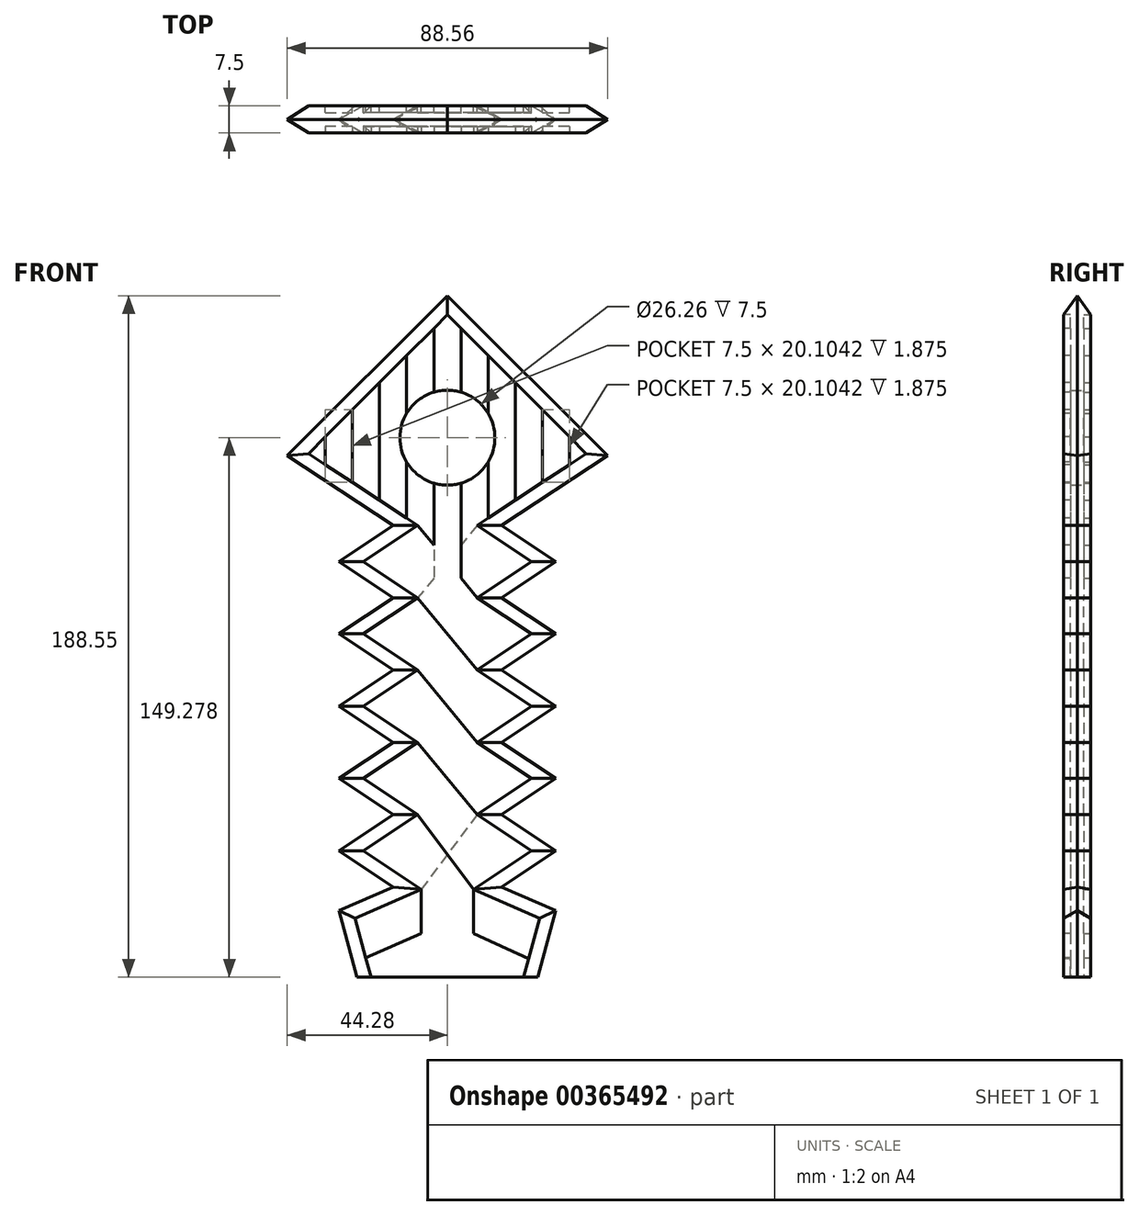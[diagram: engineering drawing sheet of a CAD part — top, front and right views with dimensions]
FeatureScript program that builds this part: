
annotation { "Feature Type Name" : "Feature", "Feature Type Description" : "" }
export const myFeature = defineFeature(function(context is Context, id is Id, definition is map)
    precondition{}
    {
        {
            var Q0;
            Q0=qCreatedBy(makeId("Front.planeOp"),FACE);
            var sketch = newSketch(context, id + "F0", { "sketchPlane" : qUnion([Q0])});
            skLineSegment(sketch, "E0", {"start": v(-15, -50) * mm, "end": v(15, -50) * mm});
            skLineSegment(sketch, "E1", {"start": v(15, -50) * mm, "end": v(15, 75) * mm});
            skLineSegment(sketch, "E2", {"start": v(-15, 75) * mm, "end": v(-15, -50) * mm});
            skLineSegment(sketch, "E3", {"start": v(15, 75) * mm, "end": v(34.28, 94.28) * mm});
            skLineSegment(sketch, "E4", {"start": v(34.28, 94.28) * mm, "end": v(0, 128.55) * mm});
            skLineSegment(sketch, "E5", {"start": v(0, 128.55) * mm, "end": v(-34.28, 94.28) * mm});
            skLineSegment(sketch, "E6", {"start": v(-15, 75) * mm, "end": v(-34.28, 94.28) * mm});
            skLineSegment(sketch, "E7", {"start": v(0, 128.55) * mm, "end": v(0, 138.55) * mm});
            skLineSegment(sketch, "E8", {"start": v(0, 138.55) * mm, "end": v(44.28, 94.28) * mm});
            skLineSegment(sketch, "E9", {"start": v(44.28, 94.28) * mm, "end": v(15, 75) * mm});
            skLineSegment(sketch, "E10", {"start": v(0, 138.55) * mm, "end": v(-44.28, 94.28) * mm});
            skLineSegment(sketch, "E11", {"start": v(-44.28, 94.28) * mm, "end": v(-15, 75) * mm});
            skLineSegment(sketch, "E12", {"start": v(-34.28, 94.28) * mm, "end": v(-44.28, 94.28) * mm});
            skLineSegment(sketch, "E13", {"start": v(34.28, 94.28) * mm, "end": v(44.28, 94.28) * mm});
            skLineSegment(sketch, "E14", {"start": v(15, 75) * mm, "end": v(25, 65) * mm});
            skLineSegment(sketch, "E15", {"start": v(25, 65) * mm, "end": v(15, 55) * mm});
            skLineSegment(sketch, "E16", {"start": v(15, 55) * mm, "end": v(25, 45) * mm});
            skLineSegment(sketch, "E17", {"start": v(25, 45) * mm, "end": v(15, 35) * mm});
            skLineSegment(sketch, "E18", {"start": v(15, 35) * mm, "end": v(25, 25) * mm});
            skLineSegment(sketch, "E19", {"start": v(25, 25) * mm, "end": v(15, 15) * mm});
            skLineSegment(sketch, "E20", {"start": v(15, 15) * mm, "end": v(25, 5) * mm});
            skLineSegment(sketch, "E21", {"start": v(25, 5) * mm, "end": v(15, -5) * mm});
            skLineSegment(sketch, "E22", {"start": v(15, -5) * mm, "end": v(25, -15) * mm});
            skLineSegment(sketch, "E23", {"start": v(25, -15) * mm, "end": v(15, -25) * mm});
            skLineSegment(sketch, "E24", {"start": v(15, 75) * mm, "end": v(30, 65) * mm});
            skLineSegment(sketch, "E25", {"start": v(30, 65) * mm, "end": v(15, 55) * mm});
            skLineSegment(sketch, "E26", {"start": v(15, 55) * mm, "end": v(30, 45) * mm});
            skLineSegment(sketch, "E27", {"start": v(30, 45) * mm, "end": v(15, 35) * mm});
            skLineSegment(sketch, "E28", {"start": v(15, 35) * mm, "end": v(30, 25) * mm});
            skLineSegment(sketch, "E29", {"start": v(30, 25) * mm, "end": v(15, 15) * mm});
            skLineSegment(sketch, "E30", {"start": v(15, 15) * mm, "end": v(30, 5) * mm});
            skLineSegment(sketch, "E31", {"start": v(30, 5) * mm, "end": v(15, -5) * mm});
            skLineSegment(sketch, "E32", {"start": v(15, -5) * mm, "end": v(30, -15) * mm});
            skLineSegment(sketch, "E33", {"start": v(30, -15) * mm, "end": v(15, -25) * mm});
            skLineSegment(sketch, "E34", {"start": v(15, -25) * mm, "end": v(30, -31.56) * mm});
            skLineSegment(sketch, "E35", {"start": v(30, -31.56) * mm, "end": v(25, -50) * mm});
            skLineSegment(sketch, "E36", {"start": v(25, -50) * mm, "end": v(15, -50) * mm});
            skLineSegment(sketch, "E37", {"start": v(-15, 75) * mm, "end": v(-25, 65) * mm});
            skLineSegment(sketch, "E38", {"start": v(-25, 65) * mm, "end": v(-15, 55) * mm});
            skLineSegment(sketch, "E39", {"start": v(-15, 55) * mm, "end": v(-25, 45) * mm});
            skLineSegment(sketch, "E40", {"start": v(-25, 45) * mm, "end": v(-15, 35) * mm});
            skLineSegment(sketch, "E41", {"start": v(-15, 35) * mm, "end": v(-25, 25) * mm});
            skLineSegment(sketch, "E42", {"start": v(-25, 25) * mm, "end": v(-15, 15) * mm});
            skLineSegment(sketch, "E43", {"start": v(-15, 15) * mm, "end": v(-25, 5) * mm});
            skLineSegment(sketch, "E44", {"start": v(-25, 5) * mm, "end": v(-15, -5) * mm});
            skLineSegment(sketch, "E45", {"start": v(-15, -5) * mm, "end": v(-25, -15) * mm});
            skLineSegment(sketch, "E46", {"start": v(-25, -15) * mm, "end": v(-15, -25) * mm});
            skLineSegment(sketch, "E47", {"start": v(-15, 75) * mm, "end": v(-30, 65) * mm});
            skLineSegment(sketch, "E48", {"start": v(-30, 65) * mm, "end": v(-15, 55) * mm});
            skLineSegment(sketch, "E49", {"start": v(-15, 55) * mm, "end": v(-30, 45) * mm});
            skLineSegment(sketch, "E50", {"start": v(-30, 45) * mm, "end": v(-15, 35) * mm});
            skLineSegment(sketch, "E51", {"start": v(-15, 35) * mm, "end": v(-30, 25) * mm});
            skLineSegment(sketch, "E52", {"start": v(-30, 25) * mm, "end": v(-15, 15) * mm});
            skLineSegment(sketch, "E53", {"start": v(-15, 15) * mm, "end": v(-30, 5) * mm});
            skLineSegment(sketch, "E54", {"start": v(-30, 5) * mm, "end": v(-15, -5) * mm});
            skLineSegment(sketch, "E55", {"start": v(-15, -5) * mm, "end": v(-30, -15) * mm});
            skLineSegment(sketch, "E56", {"start": v(-30, -15) * mm, "end": v(-15, -25) * mm});
            skLineSegment(sketch, "E57", {"start": v(-15, -25) * mm, "end": v(-30, -31.56) * mm});
            skLineSegment(sketch, "E58", {"start": v(-30, -31.56) * mm, "end": v(-25, -50) * mm});
            skLineSegment(sketch, "E59", {"start": v(-25, -50) * mm, "end": v(-15, -50) * mm});
            skCircle(sketch, "E60", {"center": v(0, 99.28) * mm, "radius": 13.13 * mm});
            skLineSegment(sketch, "E61", {"start": v(3.75, 86.7) * mm, "end": v(3.75, -50) * mm});
            skLineSegment(sketch, "E62", {"start": v(-3.75, 86.7) * mm, "end": v(-3.75, -50) * mm});
            skSolve(sketch);
        }
        {
            var Q0;
            Q0 = qSketchRegion(id + "F0", true);
            var Q1;
            Q1=makeQuery(id+"F0.imprint","IMPRINT",FACE,{"disambiguationData":[TD([[makeQuery(id+"F0.imprint","IMPRINT",EDGE,{"derivedFrom":sQuery(id+"F0.wireOp",EDGE,"tEIcV5ed-Dlti-Xe9K-ipyq-D6JpYmqXNQwO")}),-1.0]])]});
            var Q2;
            Q2=makeQuery(id+"F0.imprint","IMPRINT",FACE,{"disambiguationData":[TD([[makeQuery(id+"F0.imprint","IMPRINT",EDGE,{"derivedFrom":sQuery(id+"F0.wireOp",EDGE,"oY2jZxbk-D1su-Rdax-I2aS-zYsjSGYaF0MI")}),-1.0]])]});
            var Q3;
            Q3=makeQuery(id+"F0.imprint","IMPRINT",FACE,{"disambiguationData":[TD([[makeQuery(id+"F0.imprint","IMPRINT",EDGE,{"derivedFrom":sQuery(id+"F0.wireOp",EDGE,"hQpNWvsG-qMPW-6KJk-tWaw-b78FssZYuDap")}),-1.0]])]});
            extrude(context, id + "F1", {"entities" : qUnion([Q0, Q1, Q2, Q3]), "depth" : 7.5 * mm});
        }
        {
            var Q0;
            Q0=makeQuery(id+"F1.opExtrude","CAP_EDGE",EDGE,{"disambiguationData":[OSD([sQuery(id+"F0.wireOp",EDGE,"E10")])],"isStart":false});
            var Q1;
            Q1=makeQuery(id+"F1.opExtrude","CAP_EDGE",EDGE,{"disambiguationData":[OSD([sQuery(id+"F0.wireOp",EDGE,"E8")])],"isStart":true});
            var Q2;
            Q2=makeQuery(id+"F1.opExtrude","CAP_EDGE",EDGE,{"disambiguationData":[OSD([sQuery(id+"F0.wireOp",EDGE,"E10")])],"isStart":true});
            var Q3;
            Q3=makeQuery(id+"F1.opExtrude","CAP_EDGE",EDGE,{"disambiguationData":[OSD([sQuery(id+"F0.wireOp",EDGE,"E8")])],"isStart":false});
            var Q4;
            Q4=makeQuery(id+"F1.opExtrude","CAP_EDGE",EDGE,{"disambiguationData":[OSD([sQuery(id+"F0.wireOp",EDGE,"E9")])],"isStart":false});
            var Q5;
            Q5=makeQuery(id+"F1.opExtrude","CAP_EDGE",EDGE,{"disambiguationData":[OSD([sQuery(id+"F0.wireOp",EDGE,"E9")])],"isStart":true});
            var Q6;
            Q6=makeQuery(id+"F1.opExtrude","CAP_EDGE",EDGE,{"disambiguationData":[OSD([sQuery(id+"F0.wireOp",EDGE,"E11")])],"isStart":true});
            var Q7;
            Q7=makeQuery(id+"F1.opExtrude","CAP_EDGE",EDGE,{"disambiguationData":[OSD([sQuery(id+"F0.wireOp",EDGE,"E11")])],"isStart":false});
            var Q8;
            Q8=makeQuery(id+"F1.opExtrude","CAP_EDGE",EDGE,{"disambiguationData":[OSD([sQuery(id+"F0.wireOp",EDGE,"E24")])],"isStart":true});
            var Q9;
            Q9=makeQuery(id+"F1.opExtrude","CAP_EDGE",EDGE,{"disambiguationData":[OSD([sQuery(id+"F0.wireOp",EDGE,"E25")])],"isStart":true});
            var Q10;
            Q10=makeQuery(id+"F1.opExtrude","CAP_EDGE",EDGE,{"disambiguationData":[OSD([sQuery(id+"F0.wireOp",EDGE,"E26")])],"isStart":true});
            var Q11;
            Q11=makeQuery(id+"F1.opExtrude","CAP_EDGE",EDGE,{"disambiguationData":[OSD([sQuery(id+"F0.wireOp",EDGE,"E27")])],"isStart":true});
            var Q12;
            Q12=makeQuery(id+"F1.opExtrude","CAP_EDGE",EDGE,{"disambiguationData":[OSD([sQuery(id+"F0.wireOp",EDGE,"E28")])],"isStart":true});
            var Q13;
            Q13=makeQuery(id+"F1.opExtrude","CAP_EDGE",EDGE,{"disambiguationData":[OSD([sQuery(id+"F0.wireOp",EDGE,"E29")])],"isStart":true});
            var Q14;
            Q14=makeQuery(id+"F1.opExtrude","CAP_EDGE",EDGE,{"disambiguationData":[OSD([sQuery(id+"F0.wireOp",EDGE,"E30")])],"isStart":true});
            var Q15;
            Q15=makeQuery(id+"F1.opExtrude","CAP_EDGE",EDGE,{"disambiguationData":[OSD([sQuery(id+"F0.wireOp",EDGE,"E31")])],"isStart":true});
            var Q16;
            Q16=makeQuery(id+"F1.opExtrude","CAP_EDGE",EDGE,{"disambiguationData":[OSD([sQuery(id+"F0.wireOp",EDGE,"E32")])],"isStart":true});
            var Q17;
            Q17=makeQuery(id+"F1.opExtrude","CAP_EDGE",EDGE,{"disambiguationData":[OSD([sQuery(id+"F0.wireOp",EDGE,"E33")])],"isStart":true});
            var Q18;
            Q18=makeQuery(id+"F1.opExtrude","CAP_EDGE",EDGE,{"disambiguationData":[OSD([sQuery(id+"F0.wireOp",EDGE,"E24")])],"isStart":false});
            var Q19;
            Q19=makeQuery(id+"F1.opExtrude","CAP_EDGE",EDGE,{"disambiguationData":[OSD([sQuery(id+"F0.wireOp",EDGE,"E25")])],"isStart":false});
            var Q20;
            Q20=makeQuery(id+"F1.opExtrude","CAP_EDGE",EDGE,{"disambiguationData":[OSD([sQuery(id+"F0.wireOp",EDGE,"E26")])],"isStart":false});
            var Q21;
            Q21=makeQuery(id+"F1.opExtrude","CAP_EDGE",EDGE,{"disambiguationData":[OSD([sQuery(id+"F0.wireOp",EDGE,"E27")])],"isStart":false});
            var Q22;
            Q22=makeQuery(id+"F1.opExtrude","CAP_EDGE",EDGE,{"disambiguationData":[OSD([sQuery(id+"F0.wireOp",EDGE,"E28")])],"isStart":false});
            var Q23;
            Q23=makeQuery(id+"F1.opExtrude","CAP_EDGE",EDGE,{"disambiguationData":[OSD([sQuery(id+"F0.wireOp",EDGE,"E29")])],"isStart":false});
            var Q24;
            Q24=makeQuery(id+"F1.opExtrude","CAP_EDGE",EDGE,{"disambiguationData":[OSD([sQuery(id+"F0.wireOp",EDGE,"E30")])],"isStart":false});
            var Q25;
            Q25=makeQuery(id+"F1.opExtrude","CAP_EDGE",EDGE,{"disambiguationData":[OSD([sQuery(id+"F0.wireOp",EDGE,"E31")])],"isStart":false});
            var Q26;
            Q26=makeQuery(id+"F1.opExtrude","CAP_EDGE",EDGE,{"disambiguationData":[OSD([sQuery(id+"F0.wireOp",EDGE,"E32")])],"isStart":false});
            var Q27;
            Q27=makeQuery(id+"F1.opExtrude","CAP_EDGE",EDGE,{"disambiguationData":[OSD([sQuery(id+"F0.wireOp",EDGE,"E33")])],"isStart":false});
            var Q28;
            Q28=makeQuery(id+"F1.opExtrude","CAP_EDGE",EDGE,{"disambiguationData":[OSD([sQuery(id+"F0.wireOp",EDGE,"E47")])],"isStart":false});
            var Q29;
            Q29=makeQuery(id+"F1.opExtrude","CAP_EDGE",EDGE,{"disambiguationData":[OSD([sQuery(id+"F0.wireOp",EDGE,"E48")])],"isStart":false});
            var Q30;
            Q30=makeQuery(id+"F1.opExtrude","CAP_EDGE",EDGE,{"disambiguationData":[OSD([sQuery(id+"F0.wireOp",EDGE,"E49")])],"isStart":false});
            var Q31;
            Q31=makeQuery(id+"F1.opExtrude","CAP_EDGE",EDGE,{"disambiguationData":[OSD([sQuery(id+"F0.wireOp",EDGE,"E50")])],"isStart":false});
            var Q32;
            Q32=makeQuery(id+"F1.opExtrude","CAP_EDGE",EDGE,{"disambiguationData":[OSD([sQuery(id+"F0.wireOp",EDGE,"E51")])],"isStart":false});
            var Q33;
            Q33=makeQuery(id+"F1.opExtrude","CAP_EDGE",EDGE,{"disambiguationData":[OSD([sQuery(id+"F0.wireOp",EDGE,"E52")])],"isStart":false});
            var Q34;
            Q34=makeQuery(id+"F1.opExtrude","CAP_EDGE",EDGE,{"disambiguationData":[OSD([sQuery(id+"F0.wireOp",EDGE,"E53")])],"isStart":false});
            var Q35;
            Q35=makeQuery(id+"F1.opExtrude","CAP_EDGE",EDGE,{"disambiguationData":[OSD([sQuery(id+"F0.wireOp",EDGE,"E54")])],"isStart":false});
            var Q36;
            Q36=makeQuery(id+"F1.opExtrude","CAP_EDGE",EDGE,{"disambiguationData":[OSD([sQuery(id+"F0.wireOp",EDGE,"E55")])],"isStart":false});
            var Q37;
            Q37=makeQuery(id+"F1.opExtrude","CAP_EDGE",EDGE,{"disambiguationData":[OSD([sQuery(id+"F0.wireOp",EDGE,"E56")])],"isStart":false});
            var Q38;
            Q38=makeQuery(id+"F1.opExtrude","CAP_EDGE",EDGE,{"disambiguationData":[OSD([sQuery(id+"F0.wireOp",EDGE,"E57")])],"isStart":false});
            var Q39;
            Q39=makeQuery(id+"F1.opExtrude","CAP_EDGE",EDGE,{"disambiguationData":[OSD([sQuery(id+"F0.wireOp",EDGE,"E47")])],"isStart":true});
            var Q40;
            Q40=makeQuery(id+"F1.opExtrude","CAP_EDGE",EDGE,{"disambiguationData":[OSD([sQuery(id+"F0.wireOp",EDGE,"E48")])],"isStart":true});
            var Q41;
            Q41=makeQuery(id+"F1.opExtrude","CAP_EDGE",EDGE,{"disambiguationData":[OSD([sQuery(id+"F0.wireOp",EDGE,"E49")])],"isStart":true});
            var Q42;
            Q42=makeQuery(id+"F1.opExtrude","CAP_EDGE",EDGE,{"disambiguationData":[OSD([sQuery(id+"F0.wireOp",EDGE,"E50")])],"isStart":true});
            var Q43;
            Q43=makeQuery(id+"F1.opExtrude","CAP_EDGE",EDGE,{"disambiguationData":[OSD([sQuery(id+"F0.wireOp",EDGE,"E51")])],"isStart":true});
            var Q44;
            Q44=makeQuery(id+"F1.opExtrude","CAP_EDGE",EDGE,{"disambiguationData":[OSD([sQuery(id+"F0.wireOp",EDGE,"E52")])],"isStart":true});
            var Q45;
            Q45=makeQuery(id+"F1.opExtrude","CAP_EDGE",EDGE,{"disambiguationData":[OSD([sQuery(id+"F0.wireOp",EDGE,"E53")])],"isStart":true});
            var Q46;
            Q46=makeQuery(id+"F1.opExtrude","CAP_EDGE",EDGE,{"disambiguationData":[OSD([sQuery(id+"F0.wireOp",EDGE,"E54")])],"isStart":true});
            var Q47;
            Q47=makeQuery(id+"F1.opExtrude","CAP_EDGE",EDGE,{"disambiguationData":[OSD([sQuery(id+"F0.wireOp",EDGE,"E55")])],"isStart":true});
            var Q48;
            Q48=makeQuery(id+"F1.opExtrude","CAP_EDGE",EDGE,{"disambiguationData":[OSD([sQuery(id+"F0.wireOp",EDGE,"E56")])],"isStart":true});
            var Q49;
            Q49=makeQuery(id+"F1.opExtrude","CAP_EDGE",EDGE,{"disambiguationData":[OSD([sQuery(id+"F0.wireOp",EDGE,"E34")])],"isStart":false});
            var Q50;
            Q50=makeQuery(id+"F1.opExtrude","CAP_EDGE",EDGE,{"disambiguationData":[OSD([sQuery(id+"F0.wireOp",EDGE,"E34")])],"isStart":true});
            var Q51;
            Q51=makeQuery(id+"F1.opExtrude","CAP_EDGE",EDGE,{"disambiguationData":[OSD([sQuery(id+"F0.wireOp",EDGE,"E57")])],"isStart":true});
            var Q52;
            Q52=makeQuery(id+"F1.opExtrude","CAP_EDGE",EDGE,{"disambiguationData":[OSD([sQuery(id+"F0.wireOp",EDGE,"E58")])],"isStart":false});
            var Q53;
            Q53=makeQuery(id+"F1.opExtrude","CAP_EDGE",EDGE,{"disambiguationData":[OSD([sQuery(id+"F0.wireOp",EDGE,"E35")])],"isStart":false});
            var Q54;
            Q54=makeQuery(id+"F1.opExtrude","CAP_EDGE",EDGE,{"disambiguationData":[OSD([sQuery(id+"F0.wireOp",EDGE,"E35")])],"isStart":true});
            var Q55;
            Q55=makeQuery(id+"F1.opExtrude","CAP_EDGE",EDGE,{"disambiguationData":[OSD([sQuery(id+"F0.wireOp",EDGE,"E58")])],"isStart":true});
            chamfer(context, id + "F2", {"entities" : qUnion([Q0, Q1, Q2, Q3, Q4, Q5, Q6, Q7, Q8, Q9, Q10, Q11, Q12, Q13, Q14, Q15, Q16, Q17, Q18, Q19, Q20, Q21, Q22, Q23, Q24, Q25, Q26, Q27, Q28, Q29, Q30, Q31, Q32, Q33, Q34, Q35, Q36, Q37, Q38, Q39, Q40, Q41, Q42, Q43, Q44, Q45, Q46, Q47, Q48, Q49, Q50, Q51, Q52, Q53, Q54, Q55]), "width" : 3.75 * mm, "tangentPropagation" : true});
        }
        {
            var Q0;
            Q0=makeQuery(id+"F1.opExtrude","CAP_FACE",FACE,{"disambiguationData":[OSD([sQuery(id+"F0.wireOp",EDGE,"E0"),sQuery(id+"F0.wireOp",EDGE,"E8"),sQuery(id+"F0.wireOp",EDGE,"E9"),sQuery(id+"F0.wireOp",EDGE,"E10"),sQuery(id+"F0.wireOp",EDGE,"E11"),sQuery(id+"F0.wireOp",EDGE,"E24"),sQuery(id+"F0.wireOp",EDGE,"E25"),sQuery(id+"F0.wireOp",EDGE,"E26"),sQuery(id+"F0.wireOp",EDGE,"E27"),sQuery(id+"F0.wireOp",EDGE,"E28"),sQuery(id+"F0.wireOp",EDGE,"E29"),sQuery(id+"F0.wireOp",EDGE,"E30"),sQuery(id+"F0.wireOp",EDGE,"E31"),sQuery(id+"F0.wireOp",EDGE,"E32"),sQuery(id+"F0.wireOp",EDGE,"E33"),sQuery(id+"F0.wireOp",EDGE,"E34"),sQuery(id+"F0.wireOp",EDGE,"E35"),sQuery(id+"F0.wireOp",EDGE,"E36"),sQuery(id+"F0.wireOp",EDGE,"E47"),sQuery(id+"F0.wireOp",EDGE,"E48"),sQuery(id+"F0.wireOp",EDGE,"E49"),sQuery(id+"F0.wireOp",EDGE,"E50"),sQuery(id+"F0.wireOp",EDGE,"E51"),sQuery(id+"F0.wireOp",EDGE,"E52"),sQuery(id+"F0.wireOp",EDGE,"E53"),sQuery(id+"F0.wireOp",EDGE,"E54"),sQuery(id+"F0.wireOp",EDGE,"E55"),sQuery(id+"F0.wireOp",EDGE,"E56"),sQuery(id+"F0.wireOp",EDGE,"E57"),sQuery(id+"F0.wireOp",EDGE,"E58"),sQuery(id+"F0.wireOp",EDGE,"E59"),sQuery(id+"F0.wireOp",EDGE,"E60")])],"isStart":true});
            var sketch = newSketch(context, id + "F3", { "sketchPlane" : qUnion([Q0])});
            skLineSegment(sketch, "E63", {"start": v(3.75, 129.5) * mm, "end": v(3.75, 86.7) * mm});
            skLineSegment(sketch, "E64", {"start": v(-3.75, 129.5) * mm, "end": v(-3.75, 86.7) * mm});
            skLineSegment(sketch, "E65", {"start": v(11.25, 122) * mm, "end": v(11.25, 77.02) * mm});
            skLineSegment(sketch, "E66", {"start": v(18.75, 114.5) * mm, "end": v(18.75, 81.96) * mm});
            skLineSegment(sketch, "E67", {"start": v(26.25, 107) * mm, "end": v(26.25, 86.9) * mm});
            skLineSegment(sketch, "E68", {"start": v(-11.25, 122) * mm, "end": v(-11.25, 77.02) * mm});
            skLineSegment(sketch, "E69", {"start": v(-18.75, 114.5) * mm, "end": v(-18.75, 81.96) * mm});
            skLineSegment(sketch, "E70", {"start": v(-26.25, 107) * mm, "end": v(-26.25, 86.9) * mm});
            skLineSegment(sketch, "E71", {"start": v(-33.75, 99.5) * mm, "end": v(-33.75, 91.84) * mm});
            skLineSegment(sketch, "E72", {"start": v(33.75, 99.5) * mm, "end": v(33.75, 91.84) * mm});
            skLineSegment(sketch, "E73", {"start": v(-8.24, -5) * mm, "end": v(7.2, -25.69) * mm});
            skLineSegment(sketch, "E74", {"start": v(7.2, -25.69) * mm, "end": v(-7.2, -25.69) * mm});
            skLineSegment(sketch, "E75", {"start": v(-7.2, -25.69) * mm, "end": v(8.24, -5) * mm});
            skLineSegment(sketch, "E76", {"start": v(8.24, -5) * mm, "end": v(-8.24, 15) * mm});
            skLineSegment(sketch, "E77", {"start": v(-8.24, 15) * mm, "end": v(8.24, 35) * mm});
            skLineSegment(sketch, "E78", {"start": v(8.24, 35) * mm, "end": v(-8.24, 55) * mm});
            skLineSegment(sketch, "E79", {"start": v(-8.24, 55) * mm, "end": v(8.21, 75.02) * mm});
            skLineSegment(sketch, "E80", {"start": v(-8.21, 75.02) * mm, "end": v(8.21, 75.02) * mm});
            skLineSegment(sketch, "E81", {"start": v(-8.21, 75.02) * mm, "end": v(8.24, 55) * mm});
            skLineSegment(sketch, "E82", {"start": v(8.24, 55) * mm, "end": v(-8.24, 35) * mm});
            skLineSegment(sketch, "E83", {"start": v(-8.24, 35) * mm, "end": v(8.24, 15) * mm});
            skLineSegment(sketch, "E84", {"start": v(8.24, 15) * mm, "end": v(-8.24, -5) * mm});
            skLineSegment(sketch, "E85", {"start": v(-3.75, 86.7) * mm, "end": v(-3.75, 75.02) * mm});
            skLineSegment(sketch, "E86", {"start": v(3.75, 86.7) * mm, "end": v(3.75, 75.02) * mm});
            skLineSegment(sketch, "E87", {"start": v(-3.75, 75.02) * mm, "end": v(-3.75, 69.6) * mm});
            skLineSegment(sketch, "E88", {"start": v(3.75, 75.02) * mm, "end": v(3.75, 60.46) * mm});
            skLineSegment(sketch, "E89", {"start": v(-7.2, -50) * mm, "end": v(-7.2, -25.69) * mm});
            skLineSegment(sketch, "E90", {"start": v(7.2, -25.69) * mm, "end": v(7.2, -50) * mm});
            skLineSegment(sketch, "E91", {"start": v(7.2, -37.84) * mm, "end": v(26.06, -46.08) * mm});
            skLineSegment(sketch, "E92", {"start": v(-7.2, -37.84) * mm, "end": v(-26.06, -46.08) * mm});
            skSolve(sketch);
        }
        {
            var Q0;
            {var subQ0=sQuery(id+"F0.wireOp",EDGE,"E60");var subQ7=sQuery(id+"F3.wireOp",EDGE,"E63");var subQ9=makeQuery(id+"F1.opExtrude","CAP_EDGE",EDGE,{"disambiguationData":[OSD([subQ0])],"isStart":true});var subQ10=makeQuery(id+"F3.imprint","INTERSECT",VERTEX,{"disambiguationData":[OD(1.0)],"derivedFrom":[subQ9,subQ7]});Q0=makeQuery(id+"F3.imprint","IMPRINT",FACE,{"disambiguationData":[TD([[makeQuery(id+"F3.imprint","IMPRINT",EDGE,{"disambiguationData":[TD([[subQ10,1.0]])],"derivedFrom":subQ9}),1.0]])]});}
            var Q1;
            {var subQ7=sQuery(id+"F3.wireOp",EDGE,"E66");Q1=makeQuery(id+"F3.imprint","IMPRINT",FACE,{"disambiguationData":[TD([[makeQuery(id+"F3.imprint","IMPRINT",EDGE,{"derivedFrom":subQ7}),-1.0]])]});}
            var Q2;
            {var subQ0=sQuery(id+"F3.wireOp",EDGE,"E67");Q2=makeQuery(id+"F3.imprint","IMPRINT",FACE,{"disambiguationData":[TD([[makeQuery(id+"F3.imprint","IMPRINT",EDGE,{"derivedFrom":subQ0}),1.0]])]});}
            var Q3;
            {var subQ0=sQuery(id+"F3.wireOp",EDGE,"E69");Q3=makeQuery(id+"F3.imprint","IMPRINT",FACE,{"disambiguationData":[TD([[makeQuery(id+"F3.imprint","IMPRINT",EDGE,{"derivedFrom":subQ0}),1.0]])]});}
            var Q4;
            {var subQ0=sQuery(id+"F3.wireOp",EDGE,"E70");Q4=makeQuery(id+"F3.imprint","IMPRINT",FACE,{"disambiguationData":[TD([[makeQuery(id+"F3.imprint","IMPRINT",EDGE,{"derivedFrom":subQ0}),-1.0]])]});}
            var Q5;
            {var subQ1=sQuery(id+"F0.wireOp",EDGE,"E34");var subQ2=sQuery(id+"F0.wireOp",EDGE,"E33");var subQ3=sQuery(id+"F0.wireOp",EDGE,"E32");var subQ4=sQuery(id+"F0.wireOp",EDGE,"E31");var subQ5=makeQuery(id+"F1.opExtrude","CAP_FACE",FACE,{"disambiguationData":[OSD([sQuery(id+"F0.wireOp",EDGE,"E0"),sQuery(id+"F0.wireOp",EDGE,"E8"),sQuery(id+"F0.wireOp",EDGE,"E9"),sQuery(id+"F0.wireOp",EDGE,"E10"),sQuery(id+"F0.wireOp",EDGE,"E11"),sQuery(id+"F0.wireOp",EDGE,"E24"),sQuery(id+"F0.wireOp",EDGE,"E25"),sQuery(id+"F0.wireOp",EDGE,"E26"),sQuery(id+"F0.wireOp",EDGE,"E27"),sQuery(id+"F0.wireOp",EDGE,"E28"),sQuery(id+"F0.wireOp",EDGE,"E29"),sQuery(id+"F0.wireOp",EDGE,"E30"),subQ4,subQ3,subQ2,subQ1,sQuery(id+"F0.wireOp",EDGE,"E35"),sQuery(id+"F0.wireOp",EDGE,"E36"),sQuery(id+"F0.wireOp",EDGE,"E47"),sQuery(id+"F0.wireOp",EDGE,"E48"),sQuery(id+"F0.wireOp",EDGE,"E49"),sQuery(id+"F0.wireOp",EDGE,"E50"),sQuery(id+"F0.wireOp",EDGE,"E51"),sQuery(id+"F0.wireOp",EDGE,"E52"),sQuery(id+"F0.wireOp",EDGE,"E53"),sQuery(id+"F0.wireOp",EDGE,"E54"),sQuery(id+"F0.wireOp",EDGE,"E55"),sQuery(id+"F0.wireOp",EDGE,"E56"),sQuery(id+"F0.wireOp",EDGE,"E57"),sQuery(id+"F0.wireOp",EDGE,"E58"),sQuery(id+"F0.wireOp",EDGE,"E59"),sQuery(id+"F0.wireOp",EDGE,"E60")])],"isStart":true});var subQ6=makeQuery(id+"F2.opChamfer","BLEND_EDGE",EDGE,{"blendedFrom":[makeQuery(id+"F1.opExtrude","CAP_EDGE",EDGE,{"disambiguationData":[OSD([subQ3])],"isStart":true}),subQ5],"blendedInto":[subQ5]});Q5=makeQuery(id+"F3.imprint","IMPRINT",FACE,{"disambiguationData":[TD([[makeQuery(id+"F3.imprint","IMPRINT",EDGE,{"derivedFrom":subQ6}),1.0]])]});}
            var Q6;
            {var subQ1=sQuery(id+"F0.wireOp",EDGE,"E55");var subQ2=sQuery(id+"F0.wireOp",EDGE,"E54");var subQ3=sQuery(id+"F0.wireOp",EDGE,"E53");var subQ4=sQuery(id+"F0.wireOp",EDGE,"E52");var subQ5=makeQuery(id+"F1.opExtrude","CAP_FACE",FACE,{"disambiguationData":[OSD([sQuery(id+"F0.wireOp",EDGE,"E0"),sQuery(id+"F0.wireOp",EDGE,"E8"),sQuery(id+"F0.wireOp",EDGE,"E9"),sQuery(id+"F0.wireOp",EDGE,"E10"),sQuery(id+"F0.wireOp",EDGE,"E11"),sQuery(id+"F0.wireOp",EDGE,"E24"),sQuery(id+"F0.wireOp",EDGE,"E25"),sQuery(id+"F0.wireOp",EDGE,"E26"),sQuery(id+"F0.wireOp",EDGE,"E27"),sQuery(id+"F0.wireOp",EDGE,"E28"),sQuery(id+"F0.wireOp",EDGE,"E29"),sQuery(id+"F0.wireOp",EDGE,"E30"),sQuery(id+"F0.wireOp",EDGE,"E31"),sQuery(id+"F0.wireOp",EDGE,"E32"),sQuery(id+"F0.wireOp",EDGE,"E33"),sQuery(id+"F0.wireOp",EDGE,"E34"),sQuery(id+"F0.wireOp",EDGE,"E35"),sQuery(id+"F0.wireOp",EDGE,"E36"),sQuery(id+"F0.wireOp",EDGE,"E47"),sQuery(id+"F0.wireOp",EDGE,"E48"),sQuery(id+"F0.wireOp",EDGE,"E49"),sQuery(id+"F0.wireOp",EDGE,"E50"),sQuery(id+"F0.wireOp",EDGE,"E51"),subQ4,subQ3,subQ2,subQ1,sQuery(id+"F0.wireOp",EDGE,"E56"),sQuery(id+"F0.wireOp",EDGE,"E57"),sQuery(id+"F0.wireOp",EDGE,"E58"),sQuery(id+"F0.wireOp",EDGE,"E59"),sQuery(id+"F0.wireOp",EDGE,"E60")])],"isStart":true});var subQ9=makeQuery(id+"F2.opChamfer","BLEND_EDGE",EDGE,{"blendedFrom":[makeQuery(id+"F1.opExtrude","CAP_EDGE",EDGE,{"disambiguationData":[OSD([subQ3])],"isStart":true}),subQ5],"blendedInto":[subQ5]});Q6=makeQuery(id+"F3.imprint","IMPRINT",FACE,{"disambiguationData":[TD([[makeQuery(id+"F3.imprint","IMPRINT",EDGE,{"derivedFrom":subQ9}),1.0]])]});}
            var Q7;
            {var subQ1=sQuery(id+"F0.wireOp",EDGE,"E30");var subQ2=sQuery(id+"F0.wireOp",EDGE,"E29");var subQ3=sQuery(id+"F0.wireOp",EDGE,"E28");var subQ4=sQuery(id+"F0.wireOp",EDGE,"E27");var subQ5=makeQuery(id+"F1.opExtrude","CAP_FACE",FACE,{"disambiguationData":[OSD([sQuery(id+"F0.wireOp",EDGE,"E0"),sQuery(id+"F0.wireOp",EDGE,"E8"),sQuery(id+"F0.wireOp",EDGE,"E9"),sQuery(id+"F0.wireOp",EDGE,"E10"),sQuery(id+"F0.wireOp",EDGE,"E11"),sQuery(id+"F0.wireOp",EDGE,"E24"),sQuery(id+"F0.wireOp",EDGE,"E25"),sQuery(id+"F0.wireOp",EDGE,"E26"),subQ4,subQ3,subQ2,subQ1,sQuery(id+"F0.wireOp",EDGE,"E31"),sQuery(id+"F0.wireOp",EDGE,"E32"),sQuery(id+"F0.wireOp",EDGE,"E33"),sQuery(id+"F0.wireOp",EDGE,"E34"),sQuery(id+"F0.wireOp",EDGE,"E35"),sQuery(id+"F0.wireOp",EDGE,"E36"),sQuery(id+"F0.wireOp",EDGE,"E47"),sQuery(id+"F0.wireOp",EDGE,"E48"),sQuery(id+"F0.wireOp",EDGE,"E49"),sQuery(id+"F0.wireOp",EDGE,"E50"),sQuery(id+"F0.wireOp",EDGE,"E51"),sQuery(id+"F0.wireOp",EDGE,"E52"),sQuery(id+"F0.wireOp",EDGE,"E53"),sQuery(id+"F0.wireOp",EDGE,"E54"),sQuery(id+"F0.wireOp",EDGE,"E55"),sQuery(id+"F0.wireOp",EDGE,"E56"),sQuery(id+"F0.wireOp",EDGE,"E57"),sQuery(id+"F0.wireOp",EDGE,"E58"),sQuery(id+"F0.wireOp",EDGE,"E59"),sQuery(id+"F0.wireOp",EDGE,"E60")])],"isStart":true});var subQ9=makeQuery(id+"F2.opChamfer","BLEND_EDGE",EDGE,{"blendedFrom":[makeQuery(id+"F1.opExtrude","CAP_EDGE",EDGE,{"disambiguationData":[OSD([subQ3])],"isStart":true}),subQ5],"blendedInto":[subQ5]});Q7=makeQuery(id+"F3.imprint","IMPRINT",FACE,{"disambiguationData":[TD([[makeQuery(id+"F3.imprint","IMPRINT",EDGE,{"derivedFrom":subQ9}),1.0]])]});}
            var Q8;
            {var subQ1=sQuery(id+"F0.wireOp",EDGE,"E51");var subQ2=sQuery(id+"F0.wireOp",EDGE,"E50");var subQ3=sQuery(id+"F0.wireOp",EDGE,"E49");var subQ4=sQuery(id+"F0.wireOp",EDGE,"E48");var subQ5=makeQuery(id+"F1.opExtrude","CAP_FACE",FACE,{"disambiguationData":[OSD([sQuery(id+"F0.wireOp",EDGE,"E0"),sQuery(id+"F0.wireOp",EDGE,"E8"),sQuery(id+"F0.wireOp",EDGE,"E9"),sQuery(id+"F0.wireOp",EDGE,"E10"),sQuery(id+"F0.wireOp",EDGE,"E11"),sQuery(id+"F0.wireOp",EDGE,"E24"),sQuery(id+"F0.wireOp",EDGE,"E25"),sQuery(id+"F0.wireOp",EDGE,"E26"),sQuery(id+"F0.wireOp",EDGE,"E27"),sQuery(id+"F0.wireOp",EDGE,"E28"),sQuery(id+"F0.wireOp",EDGE,"E29"),sQuery(id+"F0.wireOp",EDGE,"E30"),sQuery(id+"F0.wireOp",EDGE,"E31"),sQuery(id+"F0.wireOp",EDGE,"E32"),sQuery(id+"F0.wireOp",EDGE,"E33"),sQuery(id+"F0.wireOp",EDGE,"E34"),sQuery(id+"F0.wireOp",EDGE,"E35"),sQuery(id+"F0.wireOp",EDGE,"E36"),sQuery(id+"F0.wireOp",EDGE,"E47"),subQ4,subQ3,subQ2,subQ1,sQuery(id+"F0.wireOp",EDGE,"E52"),sQuery(id+"F0.wireOp",EDGE,"E53"),sQuery(id+"F0.wireOp",EDGE,"E54"),sQuery(id+"F0.wireOp",EDGE,"E55"),sQuery(id+"F0.wireOp",EDGE,"E56"),sQuery(id+"F0.wireOp",EDGE,"E57"),sQuery(id+"F0.wireOp",EDGE,"E58"),sQuery(id+"F0.wireOp",EDGE,"E59"),sQuery(id+"F0.wireOp",EDGE,"E60")])],"isStart":true});var subQ9=makeQuery(id+"F2.opChamfer","BLEND_EDGE",EDGE,{"blendedFrom":[makeQuery(id+"F1.opExtrude","CAP_EDGE",EDGE,{"disambiguationData":[OSD([subQ3])],"isStart":true}),subQ5],"blendedInto":[subQ5]});Q8=makeQuery(id+"F3.imprint","IMPRINT",FACE,{"disambiguationData":[TD([[makeQuery(id+"F3.imprint","IMPRINT",EDGE,{"derivedFrom":subQ9}),1.0]])]});}
            var Q9;
            {var subQ1=sQuery(id+"F0.wireOp",EDGE,"E26");var subQ2=sQuery(id+"F0.wireOp",EDGE,"E25");var subQ3=sQuery(id+"F0.wireOp",EDGE,"E24");var subQ4=sQuery(id+"F0.wireOp",EDGE,"E9");var subQ5=makeQuery(id+"F1.opExtrude","CAP_FACE",FACE,{"disambiguationData":[OSD([sQuery(id+"F0.wireOp",EDGE,"E0"),sQuery(id+"F0.wireOp",EDGE,"E8"),subQ4,sQuery(id+"F0.wireOp",EDGE,"E10"),sQuery(id+"F0.wireOp",EDGE,"E11"),subQ3,subQ2,subQ1,sQuery(id+"F0.wireOp",EDGE,"E27"),sQuery(id+"F0.wireOp",EDGE,"E28"),sQuery(id+"F0.wireOp",EDGE,"E29"),sQuery(id+"F0.wireOp",EDGE,"E30"),sQuery(id+"F0.wireOp",EDGE,"E31"),sQuery(id+"F0.wireOp",EDGE,"E32"),sQuery(id+"F0.wireOp",EDGE,"E33"),sQuery(id+"F0.wireOp",EDGE,"E34"),sQuery(id+"F0.wireOp",EDGE,"E35"),sQuery(id+"F0.wireOp",EDGE,"E36"),sQuery(id+"F0.wireOp",EDGE,"E47"),sQuery(id+"F0.wireOp",EDGE,"E48"),sQuery(id+"F0.wireOp",EDGE,"E49"),sQuery(id+"F0.wireOp",EDGE,"E50"),sQuery(id+"F0.wireOp",EDGE,"E51"),sQuery(id+"F0.wireOp",EDGE,"E52"),sQuery(id+"F0.wireOp",EDGE,"E53"),sQuery(id+"F0.wireOp",EDGE,"E54"),sQuery(id+"F0.wireOp",EDGE,"E55"),sQuery(id+"F0.wireOp",EDGE,"E56"),sQuery(id+"F0.wireOp",EDGE,"E57"),sQuery(id+"F0.wireOp",EDGE,"E58"),sQuery(id+"F0.wireOp",EDGE,"E59"),sQuery(id+"F0.wireOp",EDGE,"E60")])],"isStart":true});var subQ9=makeQuery(id+"F2.opChamfer","BLEND_EDGE",EDGE,{"blendedFrom":[makeQuery(id+"F1.opExtrude","CAP_EDGE",EDGE,{"disambiguationData":[OSD([subQ3])],"isStart":true}),subQ5],"blendedInto":[subQ5]});Q9=makeQuery(id+"F3.imprint","IMPRINT",FACE,{"disambiguationData":[TD([[makeQuery(id+"F3.imprint","IMPRINT",EDGE,{"derivedFrom":subQ9}),1.0]])]});}
            var Q10;
            {var subQ1=sQuery(id+"F3.wireOp",EDGE,"E78");var subQ8=sQuery(id+"F3.wireOp",EDGE,"E82");var subQ9=makeQuery(id+"F3.imprint","INTERSECT",VERTEX,{"derivedFrom":[subQ1,subQ8]});Q10=makeQuery(id+"F3.imprint","IMPRINT",FACE,{"disambiguationData":[TD([[makeQuery(id+"F3.imprint","IMPRINT",EDGE,{"disambiguationData":[TD([[subQ9,-1.0]])],"derivedFrom":subQ1}),-1.0]])]});}
            var Q11;
            {var subQ1=sQuery(id+"F3.wireOp",EDGE,"E76");var subQ8=sQuery(id+"F3.wireOp",EDGE,"E84");var subQ9=makeQuery(id+"F3.imprint","INTERSECT",VERTEX,{"derivedFrom":[subQ1,subQ8]});Q11=makeQuery(id+"F3.imprint","IMPRINT",FACE,{"disambiguationData":[TD([[makeQuery(id+"F3.imprint","IMPRINT",EDGE,{"disambiguationData":[TD([[subQ9,-1.0]])],"derivedFrom":subQ1}),-1.0]])]});}
            var Q12;
            {var subQ0=sQuery(id+"F3.wireOp",EDGE,"E74");Q12=makeQuery(id+"F3.imprint","IMPRINT",FACE,{"disambiguationData":[TD([[makeQuery(id+"F3.imprint","IMPRINT",EDGE,{"derivedFrom":subQ0}),-1.0]])]});}
            var Q13;
            {var subQ0=sQuery(id+"F3.wireOp",EDGE,"E85");Q13=makeQuery(id+"F3.imprint","IMPRINT",FACE,{"disambiguationData":[TD([[makeQuery(id+"F3.imprint","IMPRINT",EDGE,{"derivedFrom":subQ0}),1.0]])]});}
            var Q14;
            {var subQ0=sQuery(id+"F3.wireOp",EDGE,"E87");Q14=makeQuery(id+"F3.imprint","IMPRINT",FACE,{"disambiguationData":[TD([[makeQuery(id+"F3.imprint","IMPRINT",EDGE,{"derivedFrom":subQ0}),1.0]])]});}
            var Q15;
            {var subQ0=sQuery(id+"F3.wireOp",EDGE,"E81");var subQ1=sQuery(id+"F3.wireOp",EDGE,"E79");var subQ2=makeQuery(id+"F3.imprint","INTERSECT",VERTEX,{"derivedFrom":[subQ1,subQ0]});Q15=makeQuery(id+"F3.imprint","IMPRINT",FACE,{"disambiguationData":[TD([[makeQuery(id+"F3.imprint","IMPRINT",EDGE,{"disambiguationData":[TD([[subQ2,-1.0]])],"derivedFrom":subQ1}),-1.0]])]});}
            var Q16;
            Q16=makeQuery(id+"F3.imprint","IMPRINT",FACE,{"disambiguationData":[TD([[makeQuery(id+"F3.imprint","IMPRINT",EDGE,{"derivedFrom":sQuery(id+"F3.wireOp",EDGE,"E74")}),1.0]])]});
            var Q17;
            {var subQ3=sQuery(id+"F3.wireOp",EDGE,"E92");Q17=makeQuery(id+"F3.imprint","IMPRINT",FACE,{"disambiguationData":[TD([[makeQuery(id+"F3.imprint","IMPRINT",EDGE,{"derivedFrom":subQ3}),1.0]])]});}
            var Q18;
            {var subQ3=sQuery(id+"F3.wireOp",EDGE,"E91");Q18=makeQuery(id+"F3.imprint","IMPRINT",FACE,{"disambiguationData":[TD([[makeQuery(id+"F3.imprint","IMPRINT",EDGE,{"derivedFrom":subQ3}),-1.0]])]});}
            extrude(context, id + "F4", {"entities" : qUnion([Q0, Q1, Q2, Q3, Q4, Q5, Q6, Q7, Q8, Q9, Q10, Q11, Q12, Q13, Q14, Q15, Q16, Q17, Q18]), "operationType" : NewBodyOperationType.REMOVE, "oppositeDirection" : true, "depth" : 1.88 * mm});
        }
        {
            var Q0;
            Q0=makeQuery(id+"F1.opExtrude","CAP_FACE",FACE,{"disambiguationData":[OSD([sQuery(id+"F0.wireOp",EDGE,"E0"),sQuery(id+"F0.wireOp",EDGE,"E8"),sQuery(id+"F0.wireOp",EDGE,"E9"),sQuery(id+"F0.wireOp",EDGE,"E10"),sQuery(id+"F0.wireOp",EDGE,"E11"),sQuery(id+"F0.wireOp",EDGE,"E24"),sQuery(id+"F0.wireOp",EDGE,"E25"),sQuery(id+"F0.wireOp",EDGE,"E26"),sQuery(id+"F0.wireOp",EDGE,"E27"),sQuery(id+"F0.wireOp",EDGE,"E28"),sQuery(id+"F0.wireOp",EDGE,"E29"),sQuery(id+"F0.wireOp",EDGE,"E30"),sQuery(id+"F0.wireOp",EDGE,"E31"),sQuery(id+"F0.wireOp",EDGE,"E32"),sQuery(id+"F0.wireOp",EDGE,"E33"),sQuery(id+"F0.wireOp",EDGE,"E34"),sQuery(id+"F0.wireOp",EDGE,"E35"),sQuery(id+"F0.wireOp",EDGE,"E36"),sQuery(id+"F0.wireOp",EDGE,"E47"),sQuery(id+"F0.wireOp",EDGE,"E48"),sQuery(id+"F0.wireOp",EDGE,"E49"),sQuery(id+"F0.wireOp",EDGE,"E50"),sQuery(id+"F0.wireOp",EDGE,"E51"),sQuery(id+"F0.wireOp",EDGE,"E52"),sQuery(id+"F0.wireOp",EDGE,"E53"),sQuery(id+"F0.wireOp",EDGE,"E54"),sQuery(id+"F0.wireOp",EDGE,"E55"),sQuery(id+"F0.wireOp",EDGE,"E56"),sQuery(id+"F0.wireOp",EDGE,"E57"),sQuery(id+"F0.wireOp",EDGE,"E58"),sQuery(id+"F0.wireOp",EDGE,"E59"),sQuery(id+"F0.wireOp",EDGE,"E60")])],"isStart":false});
            var sketch = newSketch(context, id + "F5", { "sketchPlane" : qUnion([Q0])});
            skLineSegment(sketch, "E93", {"start": v(3.75, 129.5) * mm, "end": v(3.75, 86.7) * mm});
            skLineSegment(sketch, "E94", {"start": v(-3.75, 129.5) * mm, "end": v(-3.75, 86.7) * mm});
            skLineSegment(sketch, "E95", {"start": v(11.25, 122) * mm, "end": v(11.25, 77.02) * mm});
            skLineSegment(sketch, "E96", {"start": v(18.75, 114.5) * mm, "end": v(18.75, 81.96) * mm});
            skLineSegment(sketch, "E97", {"start": v(26.25, 107) * mm, "end": v(26.25, 86.9) * mm});
            skLineSegment(sketch, "E98", {"start": v(-11.25, 122) * mm, "end": v(-11.25, 77.02) * mm});
            skLineSegment(sketch, "E99", {"start": v(-18.75, 114.5) * mm, "end": v(-18.75, 81.96) * mm});
            skLineSegment(sketch, "E100", {"start": v(-26.25, 107) * mm, "end": v(-26.25, 86.9) * mm});
            skLineSegment(sketch, "E101", {"start": v(-33.75, 99.5) * mm, "end": v(-33.75, 91.84) * mm});
            skLineSegment(sketch, "E102", {"start": v(33.75, 99.5) * mm, "end": v(33.75, 91.84) * mm});
            skLineSegment(sketch, "E103", {"start": v(-8.24, -5) * mm, "end": v(7.2, -25.69) * mm});
            skLineSegment(sketch, "E104", {"start": v(7.2, -25.69) * mm, "end": v(-7.2, -25.69) * mm});
            skLineSegment(sketch, "E105", {"start": v(-7.2, -25.69) * mm, "end": v(8.24, -5) * mm});
            skLineSegment(sketch, "E106", {"start": v(8.24, -5) * mm, "end": v(-8.24, 15) * mm});
            skLineSegment(sketch, "E107", {"start": v(-8.24, 15) * mm, "end": v(8.24, 35) * mm});
            skLineSegment(sketch, "E108", {"start": v(8.24, 35) * mm, "end": v(-8.24, 55) * mm});
            skLineSegment(sketch, "E109", {"start": v(-8.24, 55) * mm, "end": v(8.21, 75.02) * mm});
            skLineSegment(sketch, "E110", {"start": v(-8.21, 75.02) * mm, "end": v(8.21, 75.02) * mm});
            skLineSegment(sketch, "E111", {"start": v(-8.21, 75.02) * mm, "end": v(8.24, 55) * mm});
            skLineSegment(sketch, "E112", {"start": v(8.24, 55) * mm, "end": v(-8.24, 35) * mm});
            skLineSegment(sketch, "E113", {"start": v(-8.24, 35) * mm, "end": v(8.24, 15) * mm});
            skLineSegment(sketch, "E114", {"start": v(8.24, 15) * mm, "end": v(-8.24, -5) * mm});
            skLineSegment(sketch, "E115", {"start": v(-3.75, 86.7) * mm, "end": v(-3.75, 69.6) * mm});
            skLineSegment(sketch, "E116", {"start": v(3.75, 86.7) * mm, "end": v(3.75, 60.46) * mm});
            skLineSegment(sketch, "E117", {"start": v(-7.2, -25.69) * mm, "end": v(-7.2, -50) * mm});
            skLineSegment(sketch, "E118", {"start": v(-7.2, -50) * mm, "end": v(7.2, -50) * mm});
            skLineSegment(sketch, "E119", {"start": v(7.2, -50) * mm, "end": v(7.2, -25.69) * mm});
            skLineSegment(sketch, "E120", {"start": v(7.2, -37.84) * mm, "end": v(25.96, -46.47) * mm});
            skLineSegment(sketch, "E121", {"start": v(-7.2, -37.84) * mm, "end": v(-26.04, -46.16) * mm});
            skSolve(sketch);
        }
        {
            var Q0;
            {var subQ0=sQuery(id+"F0.wireOp",EDGE,"E60");var subQ9=sQuery(id+"F5.wireOp",EDGE,"E93");var subQ11=makeQuery(id+"F1.opExtrude","CAP_EDGE",EDGE,{"disambiguationData":[OSD([subQ0])],"isStart":false});var subQ12=makeQuery(id+"F5.imprint","INTERSECT",VERTEX,{"disambiguationData":[OD(1.0)],"derivedFrom":[subQ11,subQ9]});Q0=makeQuery(id+"F5.imprint","IMPRINT",FACE,{"disambiguationData":[TD([[makeQuery(id+"F5.imprint","IMPRINT",EDGE,{"disambiguationData":[TD([[subQ12,-1.0]])],"derivedFrom":subQ11}),-1.0]])]});}
            var Q1;
            {var subQ0=sQuery(id+"F5.wireOp",EDGE,"E96");Q1=makeQuery(id+"F5.imprint","IMPRINT",FACE,{"disambiguationData":[TD([[makeQuery(id+"F5.imprint","IMPRINT",EDGE,{"derivedFrom":subQ0}),-1.0]])]});}
            var Q2;
            {var subQ0=sQuery(id+"F5.wireOp",EDGE,"E97");Q2=makeQuery(id+"F5.imprint","IMPRINT",FACE,{"disambiguationData":[TD([[makeQuery(id+"F5.imprint","IMPRINT",EDGE,{"derivedFrom":subQ0}),1.0]])]});}
            var Q3;
            {var subQ7=sQuery(id+"F5.wireOp",EDGE,"E99");Q3=makeQuery(id+"F5.imprint","IMPRINT",FACE,{"disambiguationData":[TD([[makeQuery(id+"F5.imprint","IMPRINT",EDGE,{"derivedFrom":subQ7}),1.0]])]});}
            var Q4;
            {var subQ0=sQuery(id+"F5.wireOp",EDGE,"E100");Q4=makeQuery(id+"F5.imprint","IMPRINT",FACE,{"disambiguationData":[TD([[makeQuery(id+"F5.imprint","IMPRINT",EDGE,{"derivedFrom":subQ0}),-1.0]])]});}
            var Q5;
            {var subQ1=sQuery(id+"F0.wireOp",EDGE,"E49");var subQ2=sQuery(id+"F0.wireOp",EDGE,"E48");var subQ3=sQuery(id+"F0.wireOp",EDGE,"E47");var subQ4=sQuery(id+"F0.wireOp",EDGE,"E11");var subQ5=makeQuery(id+"F1.opExtrude","CAP_FACE",FACE,{"disambiguationData":[OSD([sQuery(id+"F0.wireOp",EDGE,"E0"),sQuery(id+"F0.wireOp",EDGE,"E8"),sQuery(id+"F0.wireOp",EDGE,"E9"),sQuery(id+"F0.wireOp",EDGE,"E10"),subQ4,sQuery(id+"F0.wireOp",EDGE,"E24"),sQuery(id+"F0.wireOp",EDGE,"E25"),sQuery(id+"F0.wireOp",EDGE,"E26"),sQuery(id+"F0.wireOp",EDGE,"E27"),sQuery(id+"F0.wireOp",EDGE,"E28"),sQuery(id+"F0.wireOp",EDGE,"E29"),sQuery(id+"F0.wireOp",EDGE,"E30"),sQuery(id+"F0.wireOp",EDGE,"E31"),sQuery(id+"F0.wireOp",EDGE,"E32"),sQuery(id+"F0.wireOp",EDGE,"E33"),sQuery(id+"F0.wireOp",EDGE,"E34"),sQuery(id+"F0.wireOp",EDGE,"E35"),sQuery(id+"F0.wireOp",EDGE,"E36"),subQ3,subQ2,subQ1,sQuery(id+"F0.wireOp",EDGE,"E50"),sQuery(id+"F0.wireOp",EDGE,"E51"),sQuery(id+"F0.wireOp",EDGE,"E52"),sQuery(id+"F0.wireOp",EDGE,"E53"),sQuery(id+"F0.wireOp",EDGE,"E54"),sQuery(id+"F0.wireOp",EDGE,"E55"),sQuery(id+"F0.wireOp",EDGE,"E56"),sQuery(id+"F0.wireOp",EDGE,"E57"),sQuery(id+"F0.wireOp",EDGE,"E58"),sQuery(id+"F0.wireOp",EDGE,"E59"),sQuery(id+"F0.wireOp",EDGE,"E60")])],"isStart":false});var subQ9=makeQuery(id+"F2.opChamfer","BLEND_EDGE",EDGE,{"blendedFrom":[makeQuery(id+"F1.opExtrude","CAP_EDGE",EDGE,{"disambiguationData":[OSD([subQ3])],"isStart":false}),subQ5],"blendedInto":[subQ5]});Q5=makeQuery(id+"F5.imprint","IMPRINT",FACE,{"disambiguationData":[TD([[makeQuery(id+"F5.imprint","IMPRINT",EDGE,{"derivedFrom":subQ9}),1.0]])]});}
            var Q6;
            {var subQ1=sQuery(id+"F5.wireOp",EDGE,"E108");var subQ8=sQuery(id+"F5.wireOp",EDGE,"E112");var subQ9=makeQuery(id+"F5.imprint","INTERSECT",VERTEX,{"derivedFrom":[subQ1,subQ8]});Q6=makeQuery(id+"F5.imprint","IMPRINT",FACE,{"disambiguationData":[TD([[makeQuery(id+"F5.imprint","IMPRINT",EDGE,{"disambiguationData":[TD([[subQ9,-1.0]])],"derivedFrom":subQ1}),-1.0]])]});}
            var Q7;
            {var subQ1=sQuery(id+"F0.wireOp",EDGE,"E28");var subQ2=sQuery(id+"F0.wireOp",EDGE,"E27");var subQ3=sQuery(id+"F0.wireOp",EDGE,"E26");var subQ4=sQuery(id+"F0.wireOp",EDGE,"E25");var subQ5=makeQuery(id+"F1.opExtrude","CAP_FACE",FACE,{"disambiguationData":[OSD([sQuery(id+"F0.wireOp",EDGE,"E0"),sQuery(id+"F0.wireOp",EDGE,"E8"),sQuery(id+"F0.wireOp",EDGE,"E9"),sQuery(id+"F0.wireOp",EDGE,"E10"),sQuery(id+"F0.wireOp",EDGE,"E11"),sQuery(id+"F0.wireOp",EDGE,"E24"),subQ4,subQ3,subQ2,subQ1,sQuery(id+"F0.wireOp",EDGE,"E29"),sQuery(id+"F0.wireOp",EDGE,"E30"),sQuery(id+"F0.wireOp",EDGE,"E31"),sQuery(id+"F0.wireOp",EDGE,"E32"),sQuery(id+"F0.wireOp",EDGE,"E33"),sQuery(id+"F0.wireOp",EDGE,"E34"),sQuery(id+"F0.wireOp",EDGE,"E35"),sQuery(id+"F0.wireOp",EDGE,"E36"),sQuery(id+"F0.wireOp",EDGE,"E47"),sQuery(id+"F0.wireOp",EDGE,"E48"),sQuery(id+"F0.wireOp",EDGE,"E49"),sQuery(id+"F0.wireOp",EDGE,"E50"),sQuery(id+"F0.wireOp",EDGE,"E51"),sQuery(id+"F0.wireOp",EDGE,"E52"),sQuery(id+"F0.wireOp",EDGE,"E53"),sQuery(id+"F0.wireOp",EDGE,"E54"),sQuery(id+"F0.wireOp",EDGE,"E55"),sQuery(id+"F0.wireOp",EDGE,"E56"),sQuery(id+"F0.wireOp",EDGE,"E57"),sQuery(id+"F0.wireOp",EDGE,"E58"),sQuery(id+"F0.wireOp",EDGE,"E59"),sQuery(id+"F0.wireOp",EDGE,"E60")])],"isStart":false});var subQ9=makeQuery(id+"F2.opChamfer","BLEND_EDGE",EDGE,{"blendedFrom":[makeQuery(id+"F1.opExtrude","CAP_EDGE",EDGE,{"disambiguationData":[OSD([subQ3])],"isStart":false}),subQ5],"blendedInto":[subQ5]});Q7=makeQuery(id+"F5.imprint","IMPRINT",FACE,{"disambiguationData":[TD([[makeQuery(id+"F5.imprint","IMPRINT",EDGE,{"derivedFrom":subQ9}),1.0]])]});}
            var Q8;
            {var subQ1=sQuery(id+"F0.wireOp",EDGE,"E53");var subQ2=sQuery(id+"F0.wireOp",EDGE,"E52");var subQ3=sQuery(id+"F0.wireOp",EDGE,"E51");var subQ4=sQuery(id+"F0.wireOp",EDGE,"E50");var subQ5=makeQuery(id+"F1.opExtrude","CAP_FACE",FACE,{"disambiguationData":[OSD([sQuery(id+"F0.wireOp",EDGE,"E0"),sQuery(id+"F0.wireOp",EDGE,"E8"),sQuery(id+"F0.wireOp",EDGE,"E9"),sQuery(id+"F0.wireOp",EDGE,"E10"),sQuery(id+"F0.wireOp",EDGE,"E11"),sQuery(id+"F0.wireOp",EDGE,"E24"),sQuery(id+"F0.wireOp",EDGE,"E25"),sQuery(id+"F0.wireOp",EDGE,"E26"),sQuery(id+"F0.wireOp",EDGE,"E27"),sQuery(id+"F0.wireOp",EDGE,"E28"),sQuery(id+"F0.wireOp",EDGE,"E29"),sQuery(id+"F0.wireOp",EDGE,"E30"),sQuery(id+"F0.wireOp",EDGE,"E31"),sQuery(id+"F0.wireOp",EDGE,"E32"),sQuery(id+"F0.wireOp",EDGE,"E33"),sQuery(id+"F0.wireOp",EDGE,"E34"),sQuery(id+"F0.wireOp",EDGE,"E35"),sQuery(id+"F0.wireOp",EDGE,"E36"),sQuery(id+"F0.wireOp",EDGE,"E47"),sQuery(id+"F0.wireOp",EDGE,"E48"),sQuery(id+"F0.wireOp",EDGE,"E49"),subQ4,subQ3,subQ2,subQ1,sQuery(id+"F0.wireOp",EDGE,"E54"),sQuery(id+"F0.wireOp",EDGE,"E55"),sQuery(id+"F0.wireOp",EDGE,"E56"),sQuery(id+"F0.wireOp",EDGE,"E57"),sQuery(id+"F0.wireOp",EDGE,"E58"),sQuery(id+"F0.wireOp",EDGE,"E59"),sQuery(id+"F0.wireOp",EDGE,"E60")])],"isStart":false});var subQ9=makeQuery(id+"F2.opChamfer","BLEND_EDGE",EDGE,{"blendedFrom":[makeQuery(id+"F1.opExtrude","CAP_EDGE",EDGE,{"disambiguationData":[OSD([subQ3])],"isStart":false}),subQ5],"blendedInto":[subQ5]});Q8=makeQuery(id+"F5.imprint","IMPRINT",FACE,{"disambiguationData":[TD([[makeQuery(id+"F5.imprint","IMPRINT",EDGE,{"derivedFrom":subQ9}),1.0]])]});}
            var Q9;
            {var subQ1=sQuery(id+"F5.wireOp",EDGE,"E106");var subQ8=sQuery(id+"F5.wireOp",EDGE,"E114");var subQ9=makeQuery(id+"F5.imprint","INTERSECT",VERTEX,{"derivedFrom":[subQ1,subQ8]});Q9=makeQuery(id+"F5.imprint","IMPRINT",FACE,{"disambiguationData":[TD([[makeQuery(id+"F5.imprint","IMPRINT",EDGE,{"disambiguationData":[TD([[subQ9,-1.0]])],"derivedFrom":subQ1}),-1.0]])]});}
            var Q10;
            {var subQ1=sQuery(id+"F0.wireOp",EDGE,"E32");var subQ2=sQuery(id+"F0.wireOp",EDGE,"E31");var subQ3=sQuery(id+"F0.wireOp",EDGE,"E30");var subQ4=sQuery(id+"F0.wireOp",EDGE,"E29");var subQ5=makeQuery(id+"F1.opExtrude","CAP_FACE",FACE,{"disambiguationData":[OSD([sQuery(id+"F0.wireOp",EDGE,"E0"),sQuery(id+"F0.wireOp",EDGE,"E8"),sQuery(id+"F0.wireOp",EDGE,"E9"),sQuery(id+"F0.wireOp",EDGE,"E10"),sQuery(id+"F0.wireOp",EDGE,"E11"),sQuery(id+"F0.wireOp",EDGE,"E24"),sQuery(id+"F0.wireOp",EDGE,"E25"),sQuery(id+"F0.wireOp",EDGE,"E26"),sQuery(id+"F0.wireOp",EDGE,"E27"),sQuery(id+"F0.wireOp",EDGE,"E28"),subQ4,subQ3,subQ2,subQ1,sQuery(id+"F0.wireOp",EDGE,"E33"),sQuery(id+"F0.wireOp",EDGE,"E34"),sQuery(id+"F0.wireOp",EDGE,"E35"),sQuery(id+"F0.wireOp",EDGE,"E36"),sQuery(id+"F0.wireOp",EDGE,"E47"),sQuery(id+"F0.wireOp",EDGE,"E48"),sQuery(id+"F0.wireOp",EDGE,"E49"),sQuery(id+"F0.wireOp",EDGE,"E50"),sQuery(id+"F0.wireOp",EDGE,"E51"),sQuery(id+"F0.wireOp",EDGE,"E52"),sQuery(id+"F0.wireOp",EDGE,"E53"),sQuery(id+"F0.wireOp",EDGE,"E54"),sQuery(id+"F0.wireOp",EDGE,"E55"),sQuery(id+"F0.wireOp",EDGE,"E56"),sQuery(id+"F0.wireOp",EDGE,"E57"),sQuery(id+"F0.wireOp",EDGE,"E58"),sQuery(id+"F0.wireOp",EDGE,"E59"),sQuery(id+"F0.wireOp",EDGE,"E60")])],"isStart":false});var subQ9=makeQuery(id+"F2.opChamfer","BLEND_EDGE",EDGE,{"blendedFrom":[makeQuery(id+"F1.opExtrude","CAP_EDGE",EDGE,{"disambiguationData":[OSD([subQ3])],"isStart":false}),subQ5],"blendedInto":[subQ5]});Q10=makeQuery(id+"F5.imprint","IMPRINT",FACE,{"disambiguationData":[TD([[makeQuery(id+"F5.imprint","IMPRINT",EDGE,{"derivedFrom":subQ9}),1.0]])]});}
            var Q11;
            {var subQ1=sQuery(id+"F0.wireOp",EDGE,"E57");var subQ2=sQuery(id+"F0.wireOp",EDGE,"E56");var subQ3=sQuery(id+"F0.wireOp",EDGE,"E55");var subQ4=sQuery(id+"F0.wireOp",EDGE,"E54");var subQ5=makeQuery(id+"F1.opExtrude","CAP_FACE",FACE,{"disambiguationData":[OSD([sQuery(id+"F0.wireOp",EDGE,"E0"),sQuery(id+"F0.wireOp",EDGE,"E8"),sQuery(id+"F0.wireOp",EDGE,"E9"),sQuery(id+"F0.wireOp",EDGE,"E10"),sQuery(id+"F0.wireOp",EDGE,"E11"),sQuery(id+"F0.wireOp",EDGE,"E24"),sQuery(id+"F0.wireOp",EDGE,"E25"),sQuery(id+"F0.wireOp",EDGE,"E26"),sQuery(id+"F0.wireOp",EDGE,"E27"),sQuery(id+"F0.wireOp",EDGE,"E28"),sQuery(id+"F0.wireOp",EDGE,"E29"),sQuery(id+"F0.wireOp",EDGE,"E30"),sQuery(id+"F0.wireOp",EDGE,"E31"),sQuery(id+"F0.wireOp",EDGE,"E32"),sQuery(id+"F0.wireOp",EDGE,"E33"),sQuery(id+"F0.wireOp",EDGE,"E34"),sQuery(id+"F0.wireOp",EDGE,"E35"),sQuery(id+"F0.wireOp",EDGE,"E36"),sQuery(id+"F0.wireOp",EDGE,"E47"),sQuery(id+"F0.wireOp",EDGE,"E48"),sQuery(id+"F0.wireOp",EDGE,"E49"),sQuery(id+"F0.wireOp",EDGE,"E50"),sQuery(id+"F0.wireOp",EDGE,"E51"),sQuery(id+"F0.wireOp",EDGE,"E52"),sQuery(id+"F0.wireOp",EDGE,"E53"),subQ4,subQ3,subQ2,subQ1,sQuery(id+"F0.wireOp",EDGE,"E58"),sQuery(id+"F0.wireOp",EDGE,"E59"),sQuery(id+"F0.wireOp",EDGE,"E60")])],"isStart":false});var subQ6=makeQuery(id+"F2.opChamfer","BLEND_EDGE",EDGE,{"blendedFrom":[makeQuery(id+"F1.opExtrude","CAP_EDGE",EDGE,{"disambiguationData":[OSD([subQ3])],"isStart":false}),subQ5],"blendedInto":[subQ5]});Q11=makeQuery(id+"F5.imprint","IMPRINT",FACE,{"disambiguationData":[TD([[makeQuery(id+"F5.imprint","IMPRINT",EDGE,{"derivedFrom":subQ6}),1.0]])]});}
            var Q12;
            {var subQ0=sQuery(id+"F5.wireOp",EDGE,"E104");Q12=makeQuery(id+"F5.imprint","IMPRINT",FACE,{"disambiguationData":[TD([[makeQuery(id+"F5.imprint","IMPRINT",EDGE,{"derivedFrom":subQ0}),-1.0]])]});}
            var Q13;
            {var subQ0=sQuery(id+"F5.wireOp",EDGE,"E115");var subQ1=sQuery(id+"F5.wireOp",EDGE,"E110");var subQ2=makeQuery(id+"F5.imprint","INTERSECT",VERTEX,{"derivedFrom":[subQ1,subQ0]});Q13=makeQuery(id+"F5.imprint","IMPRINT",FACE,{"disambiguationData":[TD([[makeQuery(id+"F5.imprint","IMPRINT",EDGE,{"disambiguationData":[TD([[subQ2,-1.0]])],"derivedFrom":subQ1}),1.0]])]});}
            var Q14;
            {var subQ1=sQuery(id+"F5.wireOp",EDGE,"E111");var subQ5=sQuery(id+"F5.wireOp",EDGE,"E109");var subQ6=makeQuery(id+"F5.imprint","INTERSECT",VERTEX,{"derivedFrom":[subQ5,subQ1]});Q14=makeQuery(id+"F5.imprint","IMPRINT",FACE,{"disambiguationData":[TD([[makeQuery(id+"F5.imprint","IMPRINT",EDGE,{"disambiguationData":[TD([[subQ6,-1.0]])],"derivedFrom":subQ5}),1.0]])]});}
            var Q15;
            {var subQ0=sQuery(id+"F5.wireOp",EDGE,"E111");var subQ1=sQuery(id+"F5.wireOp",EDGE,"E109");var subQ2=makeQuery(id+"F5.imprint","INTERSECT",VERTEX,{"derivedFrom":[subQ1,subQ0]});Q15=makeQuery(id+"F5.imprint","IMPRINT",FACE,{"disambiguationData":[TD([[makeQuery(id+"F5.imprint","IMPRINT",EDGE,{"disambiguationData":[TD([[subQ2,-1.0]])],"derivedFrom":subQ1}),-1.0]])]});}
            var Q16;
            {var subQ7=sQuery(id+"F5.wireOp",EDGE,"E104");Q16=makeQuery(id+"F5.imprint","IMPRINT",FACE,{"disambiguationData":[TD([[makeQuery(id+"F5.imprint","IMPRINT",EDGE,{"derivedFrom":subQ7}),1.0]])]});}
            var Q17;
            {var subQ3=sQuery(id+"F5.wireOp",EDGE,"E121");Q17=makeQuery(id+"F5.imprint","IMPRINT",FACE,{"disambiguationData":[TD([[makeQuery(id+"F5.imprint","IMPRINT",EDGE,{"derivedFrom":subQ3}),1.0]])]});}
            var Q18;
            {var subQ3=sQuery(id+"F5.wireOp",EDGE,"E120");Q18=makeQuery(id+"F5.imprint","IMPRINT",FACE,{"disambiguationData":[TD([[makeQuery(id+"F5.imprint","IMPRINT",EDGE,{"derivedFrom":subQ3}),-1.0]])]});}
            extrude(context, id + "F6", {"entities" : qUnion([Q0, Q1, Q2, Q3, Q4, Q5, Q6, Q7, Q8, Q9, Q10, Q11, Q12, Q13, Q14, Q15, Q16, Q17, Q18]), "operationType" : NewBodyOperationType.REMOVE, "oppositeDirection" : true, "depth" : 1.88 * mm});
        }
    });
